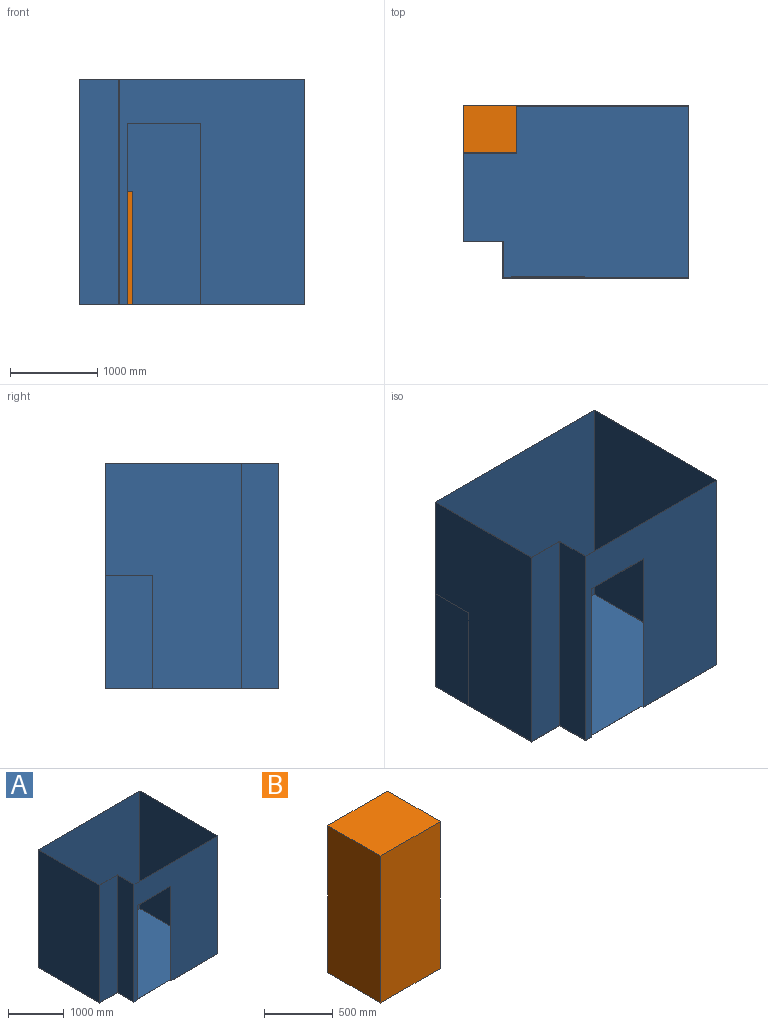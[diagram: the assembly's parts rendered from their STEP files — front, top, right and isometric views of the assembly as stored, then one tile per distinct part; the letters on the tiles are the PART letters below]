
ASSEMBLY  parts=2 mates=1
PART A: 19 faces, bbox 2590.8x1981.2x2590.8 mm
  f0: plane 2588.26x2128.52mm, normal (0,1,0), area 3765489.2mm2, adj f1,f8,f13,f14,f15,f16,f17
  f1: plane 2585.72x1976.12mm, normal (0,0,1), area 4898919.2mm2, adj f0,f10,f11,f12,f13,f14,f15,f16
  f2: plane 2590.8x2590.8mm, normal (0,1,0), area 6712244.6mm2, adj f3,f7,f8,f9
  f3: plane 2590.8x1562.1mm, normal (-1,0,0), area 4047088.7mm2, adj f2,f4,f8,f9
  f4: plane 2590.8x457.2mm, normal (0,-1,0), area 1184513.8mm2, adj f3,f5,f8,f9
  f5: plane 2590.8x419.1mm, normal (-1,0,0), area 1085804.3mm2, adj f4,f6,f8,f9
  f6: plane 2590.8x2133.6mm, normal (0,-1,0), area 3781927.9mm2, adj f5,f7,f8,f9,f15,f16,f17
  f7: plane 2590.8x1981.2mm, normal (1,0,0), area 5132893mm2, adj f2,f6,f8,f9
  f8: plane 2590.8x1981.2mm, normal (0,0,1), area 23200mm2, adj f0,f2,f3,f4,f5,f6,f7,f10
  f9: plane 2590.8x1981.2mm, normal (0,0,-1), area 4919990.2mm2, adj f2,f3,f4,f5,f6,f7,f15,f16
  f10: plane 2588.26x2585.72mm, normal (0,-1,0), area 6692515.6mm2, adj f1,f8,f11,f14
  f11: plane 2588.26x1557.02mm, normal (1,0,0), area 4029972.6mm2, adj f1,f8,f10,f12
  f12: plane 2588.26x457.2mm, normal (0,1,0), area 1183352.5mm2, adj f1,f8,f11,f13
  f13: plane 2588.26x419.1mm, normal (1,0,0), area 1084739.8mm2, adj f0,f1,f8,f12
  f14: plane 2588.26x1976.12mm, normal (-1,0,0), area 5114712.4mm2, adj f0,f1,f8,f10
  f15: plane 2082.8x25.4mm, normal (1,0,0), area 5348.4mm2, adj f0,f1,f6,f9,f17,f18
  f16: plane 2082.8x25.4mm, normal (-1,0,0), area 5348.4mm2, adj f0,f1,f6,f9,f17,f18
  f17: plane 838.2x2.54mm, normal (0,0,-1), area 2129mm2, adj f0,f6,f15,f16
  f18: plane 838.2x2.54mm, normal (0,-1,0), area 2129mm2, adj f1,f9,f15,f16
PART B: 6 faces, bbox 613.9x542x1304.3 mm
  f0: plane 1304.29x613.92mm, normal (0,1,0), area 800727.1mm2, adj f1,f3,f4,f5
  f1: plane 1304.29x542.04mm, normal (-1,0,0), area 706972.1mm2, adj f0,f2,f4,f5
  f2: plane 1304.29x613.92mm, normal (0,-1,0), area 800727.1mm2, adj f1,f3,f4,f5
  f3: plane 1304.29x542.04mm, normal (1,0,0), area 706972.1mm2, adj f0,f2,f4,f5
  f4: plane 613.92x542.04mm, normal (0,0,1), area 332765.7mm2, adj f0,f1,f2,f3
  f5: plane 613.92x542.04mm, normal (0,0,-1), area 332765.7mm2, adj f0,f1,f2,f3
PLACE A t=(-2329.06,776.68,830.99)mm
PLACE B t=(-3261.08,1676.01,830.99)mm
MATE planar B.f5 <-> A.f9  axis (0,0,-1) through (-3587.22,1950.35,830.99)mm
